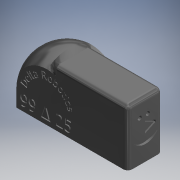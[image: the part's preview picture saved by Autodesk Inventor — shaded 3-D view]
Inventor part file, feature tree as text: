
AUTODESK INVENTOR PART (.ipt)
format: ipt  version: 2019 (Build 230136000, 136)  size: 1,033,216 bytes
history: native  units: mm (DEFAULTED — no unit token found)
features: extrude x17, sketch x15, plane x3, other x2, mirror x1, revolve x1, loft x1, fillet x1
ambient origin geometry x8: Origin, YZ Plane, XZ Plane, XY Plane, X Axis, Y Axis, Z Axis, Center Point
bodies: Solid1 (feature_tree)
feature tree (41):
  extrude  "Extrusion1"  Depth=88.9mm
  extrude  "Extrusion2"  Depth=25.4mm
  extrude  "Extrusion3"  Depth=3.175mm TaperAngle=0.0deg
  plane  "Work Plane1"
  mirror  "Mirror1"
  plane  "Work Plane2"
  revolve  "Revolution1"  [1 undecoded]
  extrude  "Extrusion5"  Depth=44.45mm
  extrude  "Extrusion8"  TaperAngle=90.0deg  [1 undecoded]
  extrude  "Extrusion9"  Depth=38.1mm
  extrude  "Extrusion10"  Depth=1.5875mm TaperAngle=0.0deg
  extrude  "Extrusion11"  Depth=3.175mm
  extrude  "Extrusion12"  Depth=19.05mm
  extrude  "Extrusion13"  Depth=12.7mm
  extrude  "Extrusion14"  Depth=71.628mm
  extrude  "Extrusion16"  Depth=16.51mm TaperAngle=0.0deg
  extrude  "Extrusion17"  Depth=3.048mm
  plane  "Work Plane6"
  extrude  "Extrusion20"  Depth=6.35mm
  extrude  "Extrusion21"  Depth=6.35mm
  extrude  "Extrusion23"  Depth=6.35mm
  extrude  "Extrusion24"  Depth=6.35mm
  loft  "Loft4"
  fillet  "Fillet4"  Radius=55.88mm
  sketch  "Sketch1"  dims[d0=82.55mm d1=88.9mm]
  sketch  "Sketch2"  dims[d2=25.4mm d3=25.4mm]
  sketch  "Sketch3"  dims[d4=59.69mm d5=0.0mm d6=3.175mm d7=0.0mm]
  sketch  "Sketch5"  dims[d8=12.7mm d9=25.4mm]
  sketch  "Sketch8"  dims[d10=9.525mm d11=0.0mm d12=44.45mm]
  sketch  "Sketch10"  dims[d13=44.45mm d14=90.0deg]
  sketch  "Sketch11"  dims[d23=2.54mm d24=0.0mm d33=38.1mm]
  sketch  "Sketch15"  dims[d34=1.27mm d35=0.0mm d36=1.5875mm d37=0.0mm]
  sketch  "Sketch16"  dims[d38=3.175mm d39=3.175mm]
  sketch  "Sketch21"  dims[d40=3.175mm d41=19.05mm]
  sketch  "Sketch22"  dims[d42=12.7mm d43=12.7mm]
  sketch  "Sketch25"  dims[d44=12.7mm d46=71.628mm]
  sketch  "Sketch26"  dims[d47=25.4mm d48=0.0mm d53=16.51mm d54=0.0mm]
  sketch  "Sketch28"  dims[d55=25.4mm d56=0.0mm d57=3.048mm]
  sketch  "Sketch29"  dims[d58=3.048mm d59=6.35mm d60=6.35mm d61=8.001mm d63=24.003mm d64=25.4mm d65=0.0mm d72=55.88mm d73=0.0mm d84=3.175mm d85=6.35mm d88=6.35mm d89=68.58mm d90=0.0mm d92=74.93mm d93=0.0mm d100=6.35mm d101=6.35mm d102=3.175mm d103=0.0mm d104=50.00625mm d105=0.0mm d109=10.16mm d110=5.08mm d111=0.0mm d112=5.08mm d113=0.0mm d114=0.0mm d115=90.0deg d116=0.0mm d117=90.0deg d118=6.35mm]
  other  "Edges6"
  other  "Edges7"
note: 2 required parameter values undecoded (feature->parameter linkage not recoverable at this tier; creation-order binding heuristic only, values carry confidence <= 0.55)